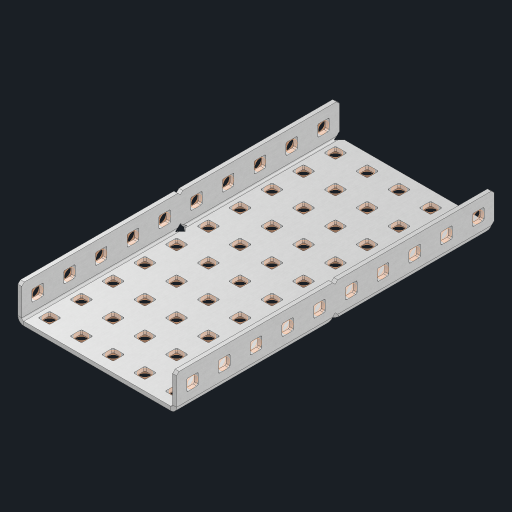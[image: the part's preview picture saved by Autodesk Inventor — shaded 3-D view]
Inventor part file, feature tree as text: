
AUTODESK INVENTOR PART (.ipt)
format: ipt  version: 2023 (Build 270158000, 158)  size: 1,032,192 bytes
history: native  units: in
note: dims shown in document units (in); Inventor stores cm internally (conversion verified against a paired STEP export)
features: other x75, extrude x69, sheet_metal_op x10, sketch x8, mirror x1, pattern_linear x1, chamfer x1
ambient origin geometry x8: Origin, YZ Plane, XZ Plane, XY Plane, X Axis, Y Axis, Z Axis, Center Point
bodies: Solid1 (feature_tree), Body (feature_tree)
feature tree (165):
  other  "Flange Pattern Plane"
  sheet_metal_op  "Flange Pattern"
  sheet_metal_op  "Body Pattern"
  other  "Arc Length"
  mirror  "Notch Mirror"
  pattern_linear  "Notch Pattern"  Spacing1=0.25in  [1 undecoded]
  chamfer  "End Chamfer"
  extrude  "Half Cut"  Depth=0.0625in
  sketch  "Sketch1"  dims[d0=2.5in]
  other  "Plate1"
  sketch  "Sketch2"  dims[d1=5.0in]
  other  "Plate2"
  sheet_metal_op  "Bend1"
  sheet_metal_op  "Corner1"
  sketch  "Sketch3"  dims[d2=0.0625in]
  other  "Flange Pattern Sketch"
  sketch  "Sketch7"  dims[d3=0.0625in]
  other  "Srf1"
  other  "Srf2"
  sketch  "Sketch8"  dims[d4=0.0312in]
  sketch  "Sketch9"  dims[d5=0.125in]
  other  "Srf91"
  sheet_metal_op  "Body Pattern Sketch"
  other  "Srf92"
  sketch  "Sketch13"  dims[d6=0.0625in]
  sketch  "Sketch14"  dims[d7=0.5in d8=90.0deg d9=0.0312in d10=0.25in d11=0.0625in d12=0.0625in d16=0.182in d17=0.02in d18=0.0625in d19=0.0in d20=0.25in d21=0.25in d46=0.172in d47=1.0in d48=0.0in d49=0.182in d50=0.02in d51=0.25in d52=0.25in d53=0.0625in d54=0.0in d55=0.172in d56=1.0in d57=0.0in d60=3.937in d62=0.5in d63=1.9685in d65=0.5in d85=0.1473in d86=0.1782in d88=0.04in d89=0.0625in d90=0.0in d91=0.04in d92=0.0491in d95=2.5in d96=0.04in d97=0.25in d98=45.0deg d101=0.0in d102=2.497in d131=2.5in d132=3.937in d134=0.5in d139=0.5in]
  other  "Srf856"
  other  "Srf1310"
  other  "Srf1311"
  other  "Srf1312"
  other  "Srf1376"
  other  "Srf1377"
  other  "Srf1728"
  other  "Srf1755"
  other  "Srf1878"
  other  "Srf1879"
  other  "Srf1880"
  other  "Srf1881"
  other  "Srf1882"
  other  "Srf1883"
  other  "Srf1884"
  other  "Srf1885"
  other  "Srf1886"
  other  "Srf1887"
  other  "Srf1888"
  other  "Srf1889"
  other  "Srf1890"
  other  "Srf1891"
  other  "Srf1942"
  other  "Srf1943"
  other  "Srf1944"
  other  "Srf1945"
  other  "Srf1946"
  other  "Srf1947"
  other  "Srf1948"
  other  "Srf1949"
  other  "Srf1950"
  other  "Srf1951"
  other  "Srf1952"
  other  "Srf1953"
  other  "Srf1954"
  other  "Srf1955"
  other  "Srf1956"
  other  "Srf1957"
  other  "Srf1958"
  other  "Srf1959"
  other  "Srf1960"
  other  "Srf1961"
  other  "Srf1962"
  other  "Srf1963"
  other  "Srf1964"
  other  "Srf1965"
  other  "Srf1966"
  other  "Srf1967"
  other  "Srf1968"
  other  "Srf1969"
  other  "Srf1970"
  other  "Srf2146"
  other  "Srf2147"
  other  "Srf2148"
  other  "Srf2149"
  other  "Srf2150"
  other  "Srf2151"
  other  "Srf2152"
  other  "Srf2153"
  other  "Srf2154"
  other  "Srf2155"
  other  "Srf2156"
  other  "Srf2157"
  other  "Srf2158"
  other  "Srf2159"
  other  "Srf2160"
  sheet_metal_op  "Flange Stamp"
  sheet_metal_op  "Flange Circle"
  sheet_metal_op  "Body Stamp"
  sheet_metal_op  "Body Circle"
  sheet_metal_op  "Notch"
  extrude  "ExtrusionSrf2"  Depth=0.0625in
  extrude  "ExtrusionSrf92"  Depth=2.5in
  extrude  "ExtrusionSrf856"  Depth=0.02in
  extrude  "ExtrusionSrf1310"  Depth=0.0625in
  extrude  "ExtrusionSrf1311"  TaperAngle=0.0deg  [1 undecoded]
  extrude  "ExtrusionSrf1312"  Depth=0.25in
  extrude  "ExtrusionSrf1376"  Depth=0.25in
  extrude  "ExtrusionSrf1377"  Depth=2.5in
  extrude  "ExtrusionSrf1728"  Depth=2.5in TaperAngle=0.0deg
  extrude  "ExtrusionSrf1755"  Depth=2.5in
  extrude  "ExtrusionSrf1878"  Depth=0.02in
  extrude  "ExtrusionSrf1879"  Depth=0.25in
  extrude  "ExtrusionSrf1880"  Depth=0.25in
  extrude  "ExtrusionSrf1881"  Depth=0.0625in
  extrude  "ExtrusionSrf1882"  TaperAngle=0.0deg  [1 undecoded]
  extrude  "ExtrusionSrf1883"  Depth=2.5in
  extrude  "ExtrusionSrf1884"  Depth=2.5in TaperAngle=0.0deg
  extrude  "ExtrusionSrf1885"  Depth=2.5in
  extrude  "ExtrusionSrf1886"  Depth=2.5in
  extrude  "ExtrusionSrf1887"  Depth=2.5in
  extrude  "ExtrusionSrf1888"  Depth=2.5in
  extrude  "ExtrusionSrf1889"  Depth=2.5in
  extrude  "ExtrusionSrf1890"  Depth=0.0625in
  extrude  "ExtrusionSrf1891"  TaperAngle=0.0deg  [1 undecoded]
  extrude  "ExtrusionSrf1942"  Depth=2.5in
  extrude  "ExtrusionSrf1943"  Depth=2.5in
  extrude  "ExtrusionSrf1944"  Depth=2.5in
  extrude  "ExtrusionSrf1945"  Depth=0.25in TaperAngle=45.0deg
  extrude  "ExtrusionSrf1946"  TaperAngle=0.0deg  [1 undecoded]
  extrude  "ExtrusionSrf1947"  Depth=2.5in
  extrude  "ExtrusionSrf1948"  Depth=2.5in
  extrude  "ExtrusionSrf1949"  Depth=2.5in
  extrude  "ExtrusionSrf1950"  Depth=2.5in
  extrude  "ExtrusionSrf1951"  Depth=2.5in
  extrude  "ExtrusionSrf1952"  [1 undecoded]
  extrude  "ExtrusionSrf1953"  [1 undecoded]
  extrude  "ExtrusionSrf1954"  [1 undecoded]
  extrude  "ExtrusionSrf1955"  [1 undecoded]
  extrude  "ExtrusionSrf1956"  [1 undecoded]
  extrude  "ExtrusionSrf1957"  [1 undecoded]
  extrude  "ExtrusionSrf1958"  [1 undecoded]
  extrude  "ExtrusionSrf1959"  [1 undecoded]
  extrude  "ExtrusionSrf1960"  [1 undecoded]
  extrude  "ExtrusionSrf1961"  [1 undecoded]
  extrude  "ExtrusionSrf1962"  [1 undecoded]
  extrude  "ExtrusionSrf1963"  [1 undecoded]
  extrude  "ExtrusionSrf1964"  [1 undecoded]
  extrude  "ExtrusionSrf1965"  [1 undecoded]
  extrude  "ExtrusionSrf1966"  [1 undecoded]
  extrude  "ExtrusionSrf1967"  [1 undecoded]
  extrude  "ExtrusionSrf1968"  [1 undecoded]
  extrude  "ExtrusionSrf1969"  [1 undecoded]
  extrude  "ExtrusionSrf1970"  [1 undecoded]
  extrude  "ExtrusionSrf2146"  [1 undecoded]
  extrude  "ExtrusionSrf2147"  [1 undecoded]
  extrude  "ExtrusionSrf2148"  [1 undecoded]
  extrude  "ExtrusionSrf2149"  [1 undecoded]
  extrude  "ExtrusionSrf2150"  [1 undecoded]
  extrude  "ExtrusionSrf2151"  [1 undecoded]
  extrude  "ExtrusionSrf2152"  [1 undecoded]
  extrude  "ExtrusionSrf2153"  [1 undecoded]
  extrude  "ExtrusionSrf2154"  [1 undecoded]
  extrude  "ExtrusionSrf2155"  [1 undecoded]
  extrude  "ExtrusionSrf2156"  [1 undecoded]
  extrude  "ExtrusionSrf2157"  [1 undecoded]
  extrude  "ExtrusionSrf2158"  [1 undecoded]
  extrude  "ExtrusionSrf2159"  [1 undecoded]
  extrude  "ExtrusionSrf2160"  [1 undecoded]
note: 39 required parameter values undecoded (feature->parameter linkage not recoverable at this tier; creation-order binding heuristic only, values carry confidence <= 0.55)
